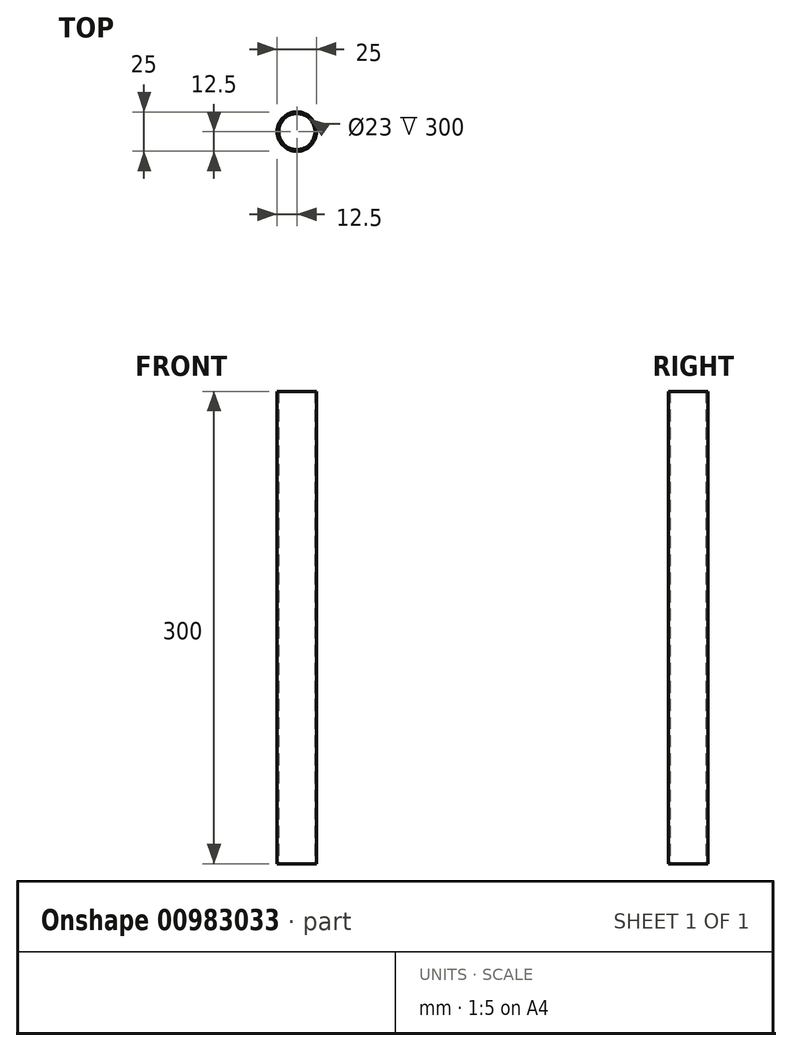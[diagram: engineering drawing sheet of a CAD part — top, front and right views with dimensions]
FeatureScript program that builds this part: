
annotation { "Feature Type Name" : "Feature", "Feature Type Description" : "" }
export const myFeature = defineFeature(function(context is Context, id is Id, definition is map)
    precondition{}
    {
        {
            var Q0;
            Q0=qCreatedBy(makeId("Top.planeOp"),FACE);
            var sketch = newSketch(context, id + "F0", { "sketchPlane" : qUnion([Q0])});
            skCircle(sketch, "E0", {"center": v(0, 0) * mm, "radius": 12.5 * mm});
            skCircle(sketch, "E1", {"center": v(0, 0) * mm, "radius": 11.5 * mm});
            skSolve(sketch);
        }
        {
            var Q0;
            Q0 = qSketchRegion(id + "F0", true);
            extrude(context, id + "F1", {"entities" : qUnion([Q0]), "depth" : 300 * mm, "offsetDistance" : 25 * mm});
        }
    });
